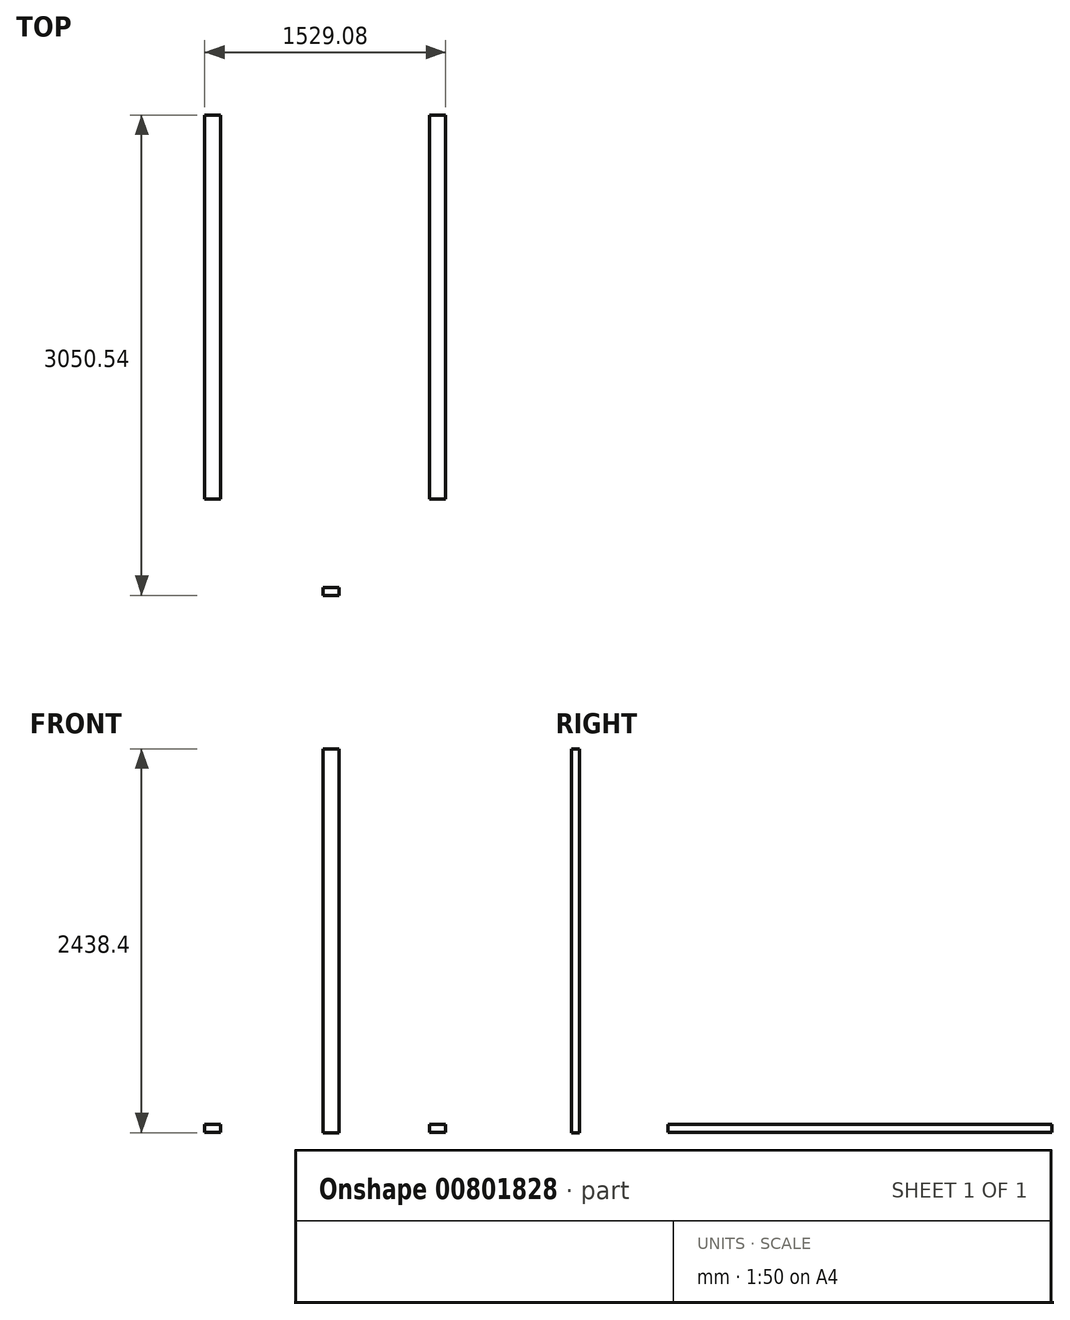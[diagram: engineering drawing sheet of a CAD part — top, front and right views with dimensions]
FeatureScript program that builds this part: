
annotation { "Feature Type Name" : "Feature", "Feature Type Description" : "" }
export const myFeature = defineFeature(function(context is Context, id is Id, definition is map)
    precondition{}
    {
        {
            var Q0;
            Q0=qCreatedBy(makeId("Front.planeOp"),FACE);
            var sketch = newSketch(context, id + "F0", { "sketchPlane" : qUnion([Q0])});
            skLineSegment(sketch, "E0.bottom", {"start": v(-93.63, 39) * mm, "end": v(7.97, 39) * mm});
            skLineSegment(sketch, "E0.top", {"start": v(-93.63, -11.8) * mm, "end": v(7.97, -11.8) * mm});
            skLineSegment(sketch, "E0.left", {"start": v(-93.63, 39) * mm, "end": v(-93.63, -11.8) * mm});
            skLineSegment(sketch, "E0.right", {"start": v(7.97, 39) * mm, "end": v(7.97, -11.8) * mm});
            skSolve(sketch);
        }
        {
            var Q0;
            Q0=makeQuery(id+"F0.imprint","IMPRINT",FACE,{"disambiguationData":[TD([[makeQuery(id+"F0.imprint","IMPRINT",EDGE,{"derivedFrom":sQuery(id+"F0.wireOp",EDGE,"E0.bottom")}),-1.0]])]});
            extrude(context, id + "F1", {"entities" : qUnion([Q0]), "depth" : 2438.4 * mm, "offsetDistance" : 25.4 * mm});
        }
        {
            var Q0;
            Q0=makeQuery(id+"F1.opExtrude","SWEPT_BODY",BODY,{"disambiguationData":[OSD([sQuery(id+"F0.wireOp",EDGE,"E0.bottom"),sQuery(id+"F0.wireOp",EDGE,"E0.top"),sQuery(id+"F0.wireOp",EDGE,"E0.left"),sQuery(id+"F0.wireOp",EDGE,"E0.right")])]});
            transform(context, id + "F2", {"entities" : qUnion([Q0]), "transformType" : TransformType.TRANSLATION_3D, "dx" : 0 * mm, "dy" : 0 * mm, "dz" : 0 * mm, "makeCopy" : true});
        }
        {
            var Q0;
            Q0=makeQuery(id+"F1.opExtrude","SWEPT_BODY",BODY,{"disambiguationData":[OSD([sQuery(id+"F0.wireOp",EDGE,"E0.bottom"),sQuery(id+"F0.wireOp",EDGE,"E0.top"),sQuery(id+"F0.wireOp",EDGE,"E0.left"),sQuery(id+"F0.wireOp",EDGE,"E0.right")])]});
            transform(context, id + "F3", {"entities" : qUnion([Q0]), "transformType" : TransformType.TRANSLATION_3D, "dx" : -1427.48 * mm, "dy" : 0 * mm, "dz" : 0 * mm, "makeCopy" : false});
        }
        {
            var Q0;
            Q0=makeQuery(id+"F1.opExtrude","SWEPT_BODY",BODY,{"disambiguationData":[OSD([sQuery(id+"F0.wireOp",EDGE,"E0.bottom"),sQuery(id+"F0.wireOp",EDGE,"E0.top"),sQuery(id+"F0.wireOp",EDGE,"E0.left"),sQuery(id+"F0.wireOp",EDGE,"E0.right")])]});
            transform(context, id + "F4", {"entities" : qUnion([Q0]), "transformType" : TransformType.TRANSLATION_3D, "dx" : 751.84 * mm, "dy" : -612.14 * mm, "dz" : 0 * mm, "makeCopy" : true});
        }
        {
            var Q0;
            Q0=makeQuery(id+"F4.opPattern","COPY",BODY,{"derivedFrom":makeQuery(id+"F1.opExtrude","SWEPT_BODY",BODY,{"disambiguationData":[OSD([sQuery(id+"F0.wireOp",EDGE,"E0.bottom"),sQuery(id+"F0.wireOp",EDGE,"E0.top"),sQuery(id+"F0.wireOp",EDGE,"E0.left"),sQuery(id+"F0.wireOp",EDGE,"E0.right")])]}),"instanceName":"1"});
            var Q1;
            Q1=makeQuery(id+"F4.opPattern","COPY",EDGE,{"derivedFrom":makeQuery(id+"F1.opExtrude","CAP_EDGE",EDGE,{"disambiguationData":[OSD([sQuery(id+"F0.wireOp",EDGE,"E0.bottom")])],"isStart":false}),"instanceName":"1"});
            transform(context, id + "F5", {"entities" : qUnion([Q0]), "transformType" : TransformType.ROTATION, "transformAxis" : qUnion([Q1]), "angle" : 90 * degree, "makeCopy" : false});
        }
        {
            var Q0;
            Q0=makeQuery(id+"F4.opPattern","COPY",BODY,{"derivedFrom":makeQuery(id+"F1.opExtrude","SWEPT_BODY",BODY,{"disambiguationData":[OSD([sQuery(id+"F0.wireOp",EDGE,"E0.bottom"),sQuery(id+"F0.wireOp",EDGE,"E0.top"),sQuery(id+"F0.wireOp",EDGE,"E0.left"),sQuery(id+"F0.wireOp",EDGE,"E0.right")])]}),"instanceName":"1"});
            transform(context, id + "F6", {"entities" : qUnion([Q0]), "transformType" : TransformType.TRANSLATION_3D, "dx" : 0 * mm, "dy" : 0 * mm, "dz" : -40.64 * mm, "makeCopy" : false});
        }
        {
            var Q0;
            Q0=makeQuery(id+"F1.opExtrude","SWEPT_BODY",BODY,{"disambiguationData":[OSD([sQuery(id+"F0.wireOp",EDGE,"E0.bottom"),sQuery(id+"F0.wireOp",EDGE,"E0.top"),sQuery(id+"F0.wireOp",EDGE,"E0.left"),sQuery(id+"F0.wireOp",EDGE,"E0.right")])]});
            transform(context, id + "F7", {"entities" : qUnion([Q0]), "transformType" : TransformType.TRANSLATION_3D, "dx" : 0 * mm, "dy" : 0 * mm, "dz" : 12.7 * mm, "makeCopy" : false});
        }
        {
            var Q0;
            Q0=makeQuery(id+"F2.opPattern","COPY",BODY,{"derivedFrom":makeQuery(id+"F1.opExtrude","SWEPT_BODY",BODY,{"disambiguationData":[OSD([sQuery(id+"F0.wireOp",EDGE,"E0.bottom"),sQuery(id+"F0.wireOp",EDGE,"E0.top"),sQuery(id+"F0.wireOp",EDGE,"E0.left"),sQuery(id+"F0.wireOp",EDGE,"E0.right")])]}),"instanceName":"1"});
            transform(context, id + "F8", {"entities" : qUnion([Q0]), "transformType" : TransformType.TRANSLATION_3D, "dx" : 0 * mm, "dy" : 0 * mm, "dz" : 12.7 * mm, "makeCopy" : false});
        }
    });
